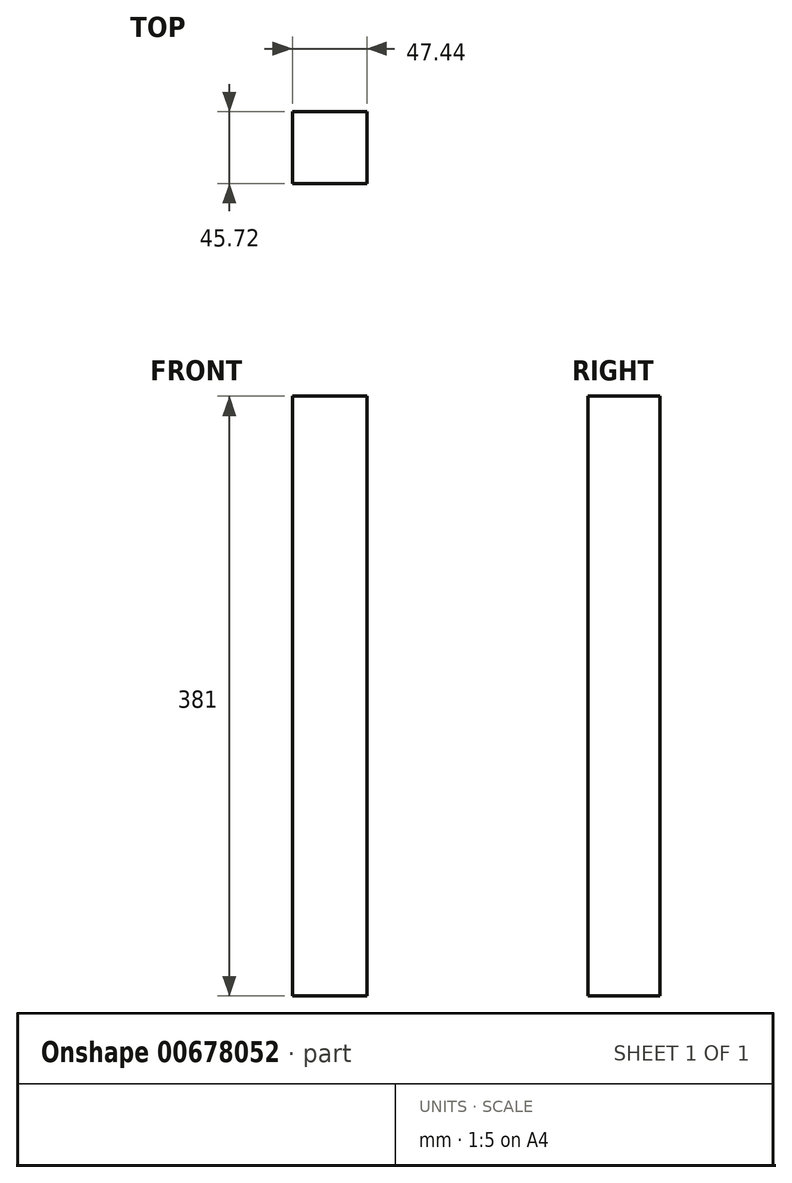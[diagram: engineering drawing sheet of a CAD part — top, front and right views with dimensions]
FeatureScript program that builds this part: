
annotation { "Feature Type Name" : "Feature", "Feature Type Description" : "" }
export const myFeature = defineFeature(function(context is Context, id is Id, definition is map)
    precondition{}
    {
        {
            var Q0;
            Q0=qCreatedBy(makeId("Top.planeOp"),FACE);
            var sketch = newSketch(context, id + "F0", { "sketchPlane" : qUnion([Q0])});
            skLineSegment(sketch, "E0.bottom", {"start": v(23.72, 22.86) * mm, "end": v(-23.72, 22.86) * mm});
            skLineSegment(sketch, "E0.top", {"start": v(23.72, -22.86) * mm, "end": v(-23.72, -22.86) * mm});
            skLineSegment(sketch, "E0.left", {"start": v(23.72, 22.86) * mm, "end": v(23.72, -22.86) * mm});
            skLineSegment(sketch, "E0.right", {"start": v(-23.72, 22.86) * mm, "end": v(-23.72, -22.86) * mm});
            skPoint(sketch, "E0.middle", {"position": v(0, 0) * mm});
            skSolve(sketch);
        }
        {
            var Q0;
            Q0=makeQuery(id+"F0.imprint","IMPRINT",FACE,{"disambiguationData":[TD([[makeQuery(id+"F0.imprint","IMPRINT",EDGE,{"derivedFrom":sQuery(id+"F0.wireOp",EDGE,"E0.bottom")}),1.0]])]});
            extrude(context, id + "F1", {"entities" : qUnion([Q0]), "depth" : 381 * mm, "offsetDistance" : 25.4 * mm});
        }
    });
